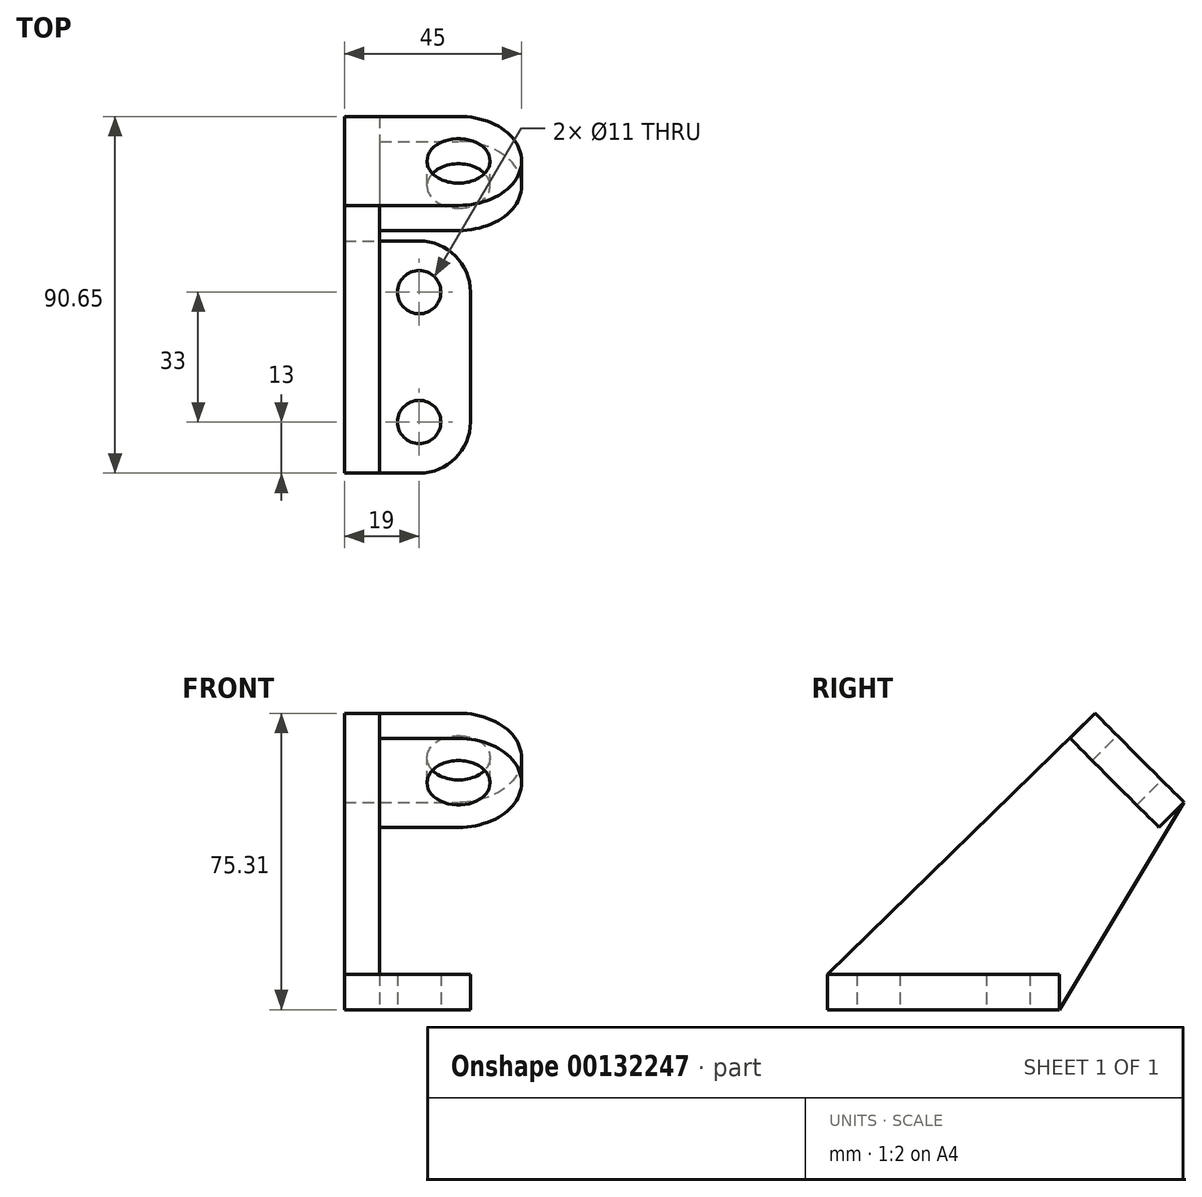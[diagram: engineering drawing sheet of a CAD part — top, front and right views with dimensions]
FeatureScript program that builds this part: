
annotation { "Feature Type Name" : "Feature", "Feature Type Description" : "" }
export const myFeature = defineFeature(function(context is Context, id is Id, definition is map)
    precondition{}
    {
        {
            var Q0;
            Q0=qCreatedBy(makeId("Top.planeOp"),FACE);
            var sketch = newSketch(context, id + "F0", { "sketchPlane" : qUnion([Q0])});
            skLineSegment(sketch, "E0.bottom", {"start": v(0, 0) * mm, "end": v(10, 0) * mm});
            skLineSegment(sketch, "E0.top", {"start": v(0, 59) * mm, "end": v(10, 59) * mm});
            skLineSegment(sketch, "E0.left", {"start": v(0, 0) * mm, "end": v(0, 59) * mm});
            skLineSegment(sketch, "E0.right", {"start": v(23, 13) * mm, "end": v(23, 46) * mm});
            skCircle(sketch, "E1", {"center": v(10, 13) * mm, "radius": 5.5 * mm});
            skCircle(sketch, "E2", {"center": v(10, 46) * mm, "radius": 5.5 * mm});
            skPoint(sketch, "E3.visualSharp", {"position": v(23, 0) * mm});
            skArc(sketch, "E3.filletArc", {"start": v(10, 0) * mm, "mid": v(19.2, 3.8) * mm, "end": v(23, 13) * mm});
            skPoint(sketch, "E4.visualSharp", {"position": v(23, 59) * mm});
            skArc(sketch, "E4.filletArc", {"start": v(23, 46) * mm, "mid": v(19.2, 55.2) * mm, "end": v(10, 59) * mm});
            skSolve(sketch);
        }
        {
            var Q0;
            Q0 = qSketchRegion(id + "F0", true);
            extrude(context, id + "F1", {"entities" : qUnion([Q0]), "depth" : 9 * mm});
        }
        {
            var Q0;
            Q0=qCreatedBy(makeId("Right.planeOp"),FACE);
            var sketch = newSketch(context, id + "F2", { "sketchPlane" : qUnion([Q0])});
            skLineSegment(sketch, "E5", {"start": v(68.03, 75.31) * mm, "end": v(90.65, 52.69) * mm});
            skLineSegment(sketch, "E6", {"start": v(90.65, 52.69) * mm, "end": v(59, 0) * mm});
            skLineSegment(sketch, "E7", {"start": v(79.34, 64) * mm, "end": v(131.26, 64) * mm, "construction": true});
            skLineSegment(sketch, "E8", {"start": v(68.03, 75.31) * mm, "end": v(0, 9) * mm});
            skLineSegment(sketch, "E9", {"start": v(0, 9) * mm, "end": v(0, 0) * mm});
            skLineSegment(sketch, "E10", {"start": v(0, 0) * mm, "end": v(59, 0) * mm});
            skSolve(sketch);
        }
        {
            var Q0;
            Q0 = qSketchRegion(id + "F2", true);
            extrude(context, id + "F3", {"entities" : qUnion([Q0]), "operationType" : NewBodyOperationType.ADD, "oppositeDirection" : true, "depth" : 9 * mm});
        }
        {
            var Q0;
            Q0=makeQuery(id+"F3.opExtrude","SWEPT_FACE",FACE,{"disambiguationData":[OSD([sQuery(id+"F2.wireOp",EDGE,"E5")])]});
            var sketch = newSketch(context, id + "F4", { "sketchPlane" : qUnion([Q0])});
            skLineSegment(sketch, "E11", {"start": v(9, 5.15) * mm, "end": v(-20, 5.15) * mm});
            skLineSegment(sketch, "E12", {"start": v(9, -26.85) * mm, "end": v(-20, -26.85) * mm});
            skLineSegment(sketch, "E13", {"start": v(9, 5.15) * mm, "end": v(9, -26.85) * mm});
            skArc(sketch, "E14", {"start": v(-20, 5.15) * mm, "mid": v(-36, -10.85) * mm, "end": v(-20, -26.85) * mm});
            skCircle(sketch, "E15", {"center": v(-20, -10.85) * mm, "radius": 8 * mm});
            skSolve(sketch);
        }
        {
            var Q0;
            Q0 = qSketchRegion(id + "F4", true);
            extrude(context, id + "F5", {"entities" : qUnion([Q0]), "operationType" : NewBodyOperationType.ADD, "oppositeDirection" : true, "depth" : 9 * mm});
        }
    });
